# Revit family: VLN_NimbusLook_F3204_BIM_NL
name_source: partatom
category: Plumbing Fixtures
revit_build: Autodesk Revit MEP 2014 (Build: 20130308_1515(x64)
units: mm (PartAtom-declared; Revit-internal decimal feet)

## types (1)
- F3204AA - NIMBUS LOOK WASTMENGKRAAN 5L/M M/KETTING
    Accessories = www.idealstandardnederland.nl
    AreaUnits = millimeters
    Assembly Code = C1030200
    AssetType = Vast
    BIMObjectName = VLN_Venlo_WashbasinTaps_F3204AA
    BREEAMApproved = No
    BarCode = 3800861046523
    Brand = Venlo
    CWFU = 0
    CodePerformance = EN 817, DIN 4109
    Color = Chroom
    ConnectionType = Sanitair
    Cost = 0 $
    Default Elevation = 800 mm  [stored 2.62467 ft]
    Description = Venlo Nimbus Look wastafelmengkraan 5 l/min DN 15. Met inzinkbare ketting. Vaste uitloop met straalregelaar. Sprong 101 mm. Hoogte uitloop 70 mm. Flexibele aansluitslangen G3/8". Metalen greep. Onderbevestiging (EASY FIX). Cartouche met keramische schijven. Bevestiging greep op de cartouche d.m.v. een RVS overbrengingspen. Draaibereik 90°. Geïntegreerd vetreservoir. Drukafhankelijke temperatuur instelling. Uithoudingstest EN 817. Geluidsniveau volgens norm DIN 4109, Groep 1.
    DurationUnit = jaar
    ECA = No
    ExpectedLife = 25
    FaucetFunction = Mengkraan
    FaucetOperation = Eenhendel
    FaucetType = Wastafelmengkraan
    Features = Wastafelmengkraan 5 l/min DN 15. Met inzinkbare ketting. Vaste uitloop met straalregelaar. Sprong 101 mm. Hoogte uitloop 70 mm. Flexibele aansluitslangen G3/8". Metalen greep. Onderbevestiging (EASY FIX). Cartouche met keramische schijven. Bevestiging greep op de cartouche d.m.v. een RVS overbrengingspen. Draaibereik 90°. Geïntegreerd vetreservoir. Drukafhankelijke temperatuur instelling. Uithoudingstest EN 817. Geluidsniveau volgens norm DIN 4109, Groep 1.
    Finish = Chroom
    FlowRate = 5 liter @ 3 bar
    HWFU = 0
    IfcExportAs = IfcValveType
    IfcExportType = FAUCET
    InstallationInstructions = http://www.idealstandardnederland.nl
    LinearUnits = millimeters
    ManufacturerURL = www.idealstandardnederland.nl
    Material = Messing
    Model = F3204AA
    ModelNumber = F3204AA
    ModelReference = Venlo Nimbus Look wastafelmengkraan 5 l/min DN 15. Met inzinkbare ketting. Vaste uitloop met straalregelaar. Sprong 101 mm. Hoogte uitloop 70 mm. Flexibele aansluitslangen G3/8". Metalen greep. Onderbevestiging (EASY FIX). Cartouche met keramische schijven. Bevestiging greep op de cartouche d.m.v. een RVS overbrengingspen. Draaibereik 90°. Geïntegreerd vetreservoir. Drukafhankelijke temperatuur instelling. Uithoudingstest EN 817. Geluidsniveau volgens norm DIN 4109, Groep 1.
    NBSDescription = Water supply fittings for washbasins and troughs
    NBSReference = 45-35-70/371
    Name = WashbasinTaps_F3204AA_Venlo
    NettWeight = 1.462 kg
    NominalHeight = 137 mm
    NominalLength = 137 mm
    NominalWidth = 49 mm
    ProductInformation = http://www.idealstandardnederland.nl
    Shape = Gesculptuurd
    Size = 49 x 137 x 137 mm
    Space = Internal
    SpareParts = www.idealstandardnederland.nl
    TMV3 = Yes
    TestPressure = 10 Bar
    URL = www.idealstandardnederland.nl
    Uniclass2015Code = Pr_40_20_87_98
    Uniclass2015Title = Washbasin taps
    Uniclass2015Version = Products v1.1
    ValveMechanism = Keramische schijven
    ValveOperation = Eenhendel
    Version = 1
    VolumeUnits = liter
    WFU = 0
    WRAS = No
    WarrantyDescription = Fabrieksgarantie
    WarrantyDurationParts = 10
    WarrantyDurationUnit = jaar
    WaterEfficientProduct = No
    WorkingPressure = 1-5 bar

note: [stored X ft] marks values corroborated as IEEE doubles in the binary element streams (Revit-internal decimal feet)

## geometry (parser evidence)
native form markers: Sweep x1
no freeform markers — native parametric forms only
